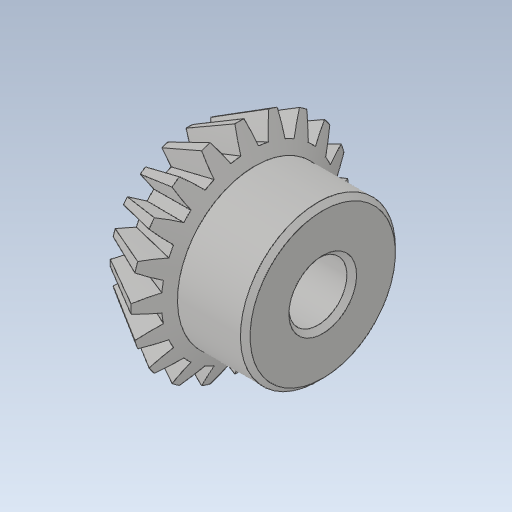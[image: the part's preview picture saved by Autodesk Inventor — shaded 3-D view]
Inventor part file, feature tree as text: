
AUTODESK INVENTOR PART (.ipt)
format: ipt  version: 2024 (Build 280153000, 153)  size: 550,400 bytes
history: native  units: mm
features: other x14, sketch x4, revolve x2, loft x1
ambient origin geometry x8: Origin, YZ Plane, XZ Plane, XY Plane, X Axis, Y Axis, Z Axis, Center Point
bodies: Solid1 (feature_tree)
feature tree (21):
  loft  "Loft1"
  revolve  "Revolution1"  Angle=360.0deg
  revolve  "Revolution2"  [1 undecoded]
  other  "IP2_XY"
  other  "IP2_YZ"
  other  "IP2_ZX"
  other  "IP2_X"
  other  "IP2_Y"
  other  "IP2_Z"
  other  "IP2_Center"
  other  "l_XY"
  other  "l_YZ"
  other  "l_ZX"
  other  "l_X"
  other  "l_Y"
  other  "l_Z"
  other  "l_Center"
  sketch  "Sketch_4"  dims[d0=0.0mm d1=90.0deg d2=0.0mm d3=90.0deg]
  sketch  "Sketch_5"  dims[d4=360.0deg d5=360.0deg]
  sketch  "Sketch_6"
  sketch  "Sketch_7"
note: 1 required parameter value undecoded (feature->parameter linkage not recoverable at this tier; creation-order binding heuristic only, values carry confidence <= 0.55)
